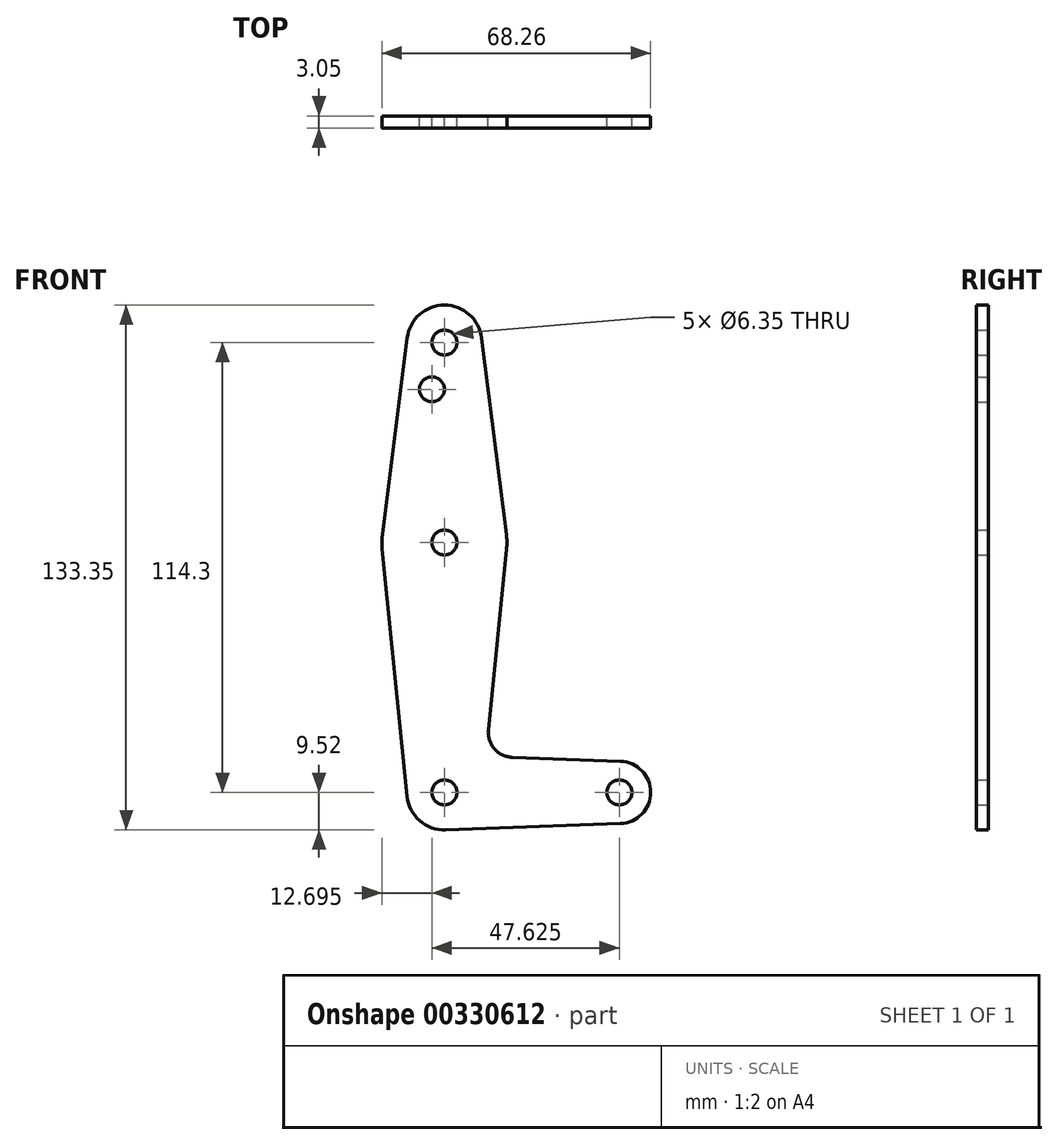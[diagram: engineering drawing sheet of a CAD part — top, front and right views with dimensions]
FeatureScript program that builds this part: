
annotation { "Feature Type Name" : "Feature", "Feature Type Description" : "" }
export const myFeature = defineFeature(function(context is Context, id is Id, definition is map)
    precondition{}
    {
        {
            var Q0;
            Q0=qCreatedBy(makeId("Front.planeOp"),FACE);
            var sketch = newSketch(context, id + "F0", { "sketchPlane" : qUnion([Q0])});
            skLineSegment(sketch, "E0", {"start": v(0, 114.3) * mm, "end": v(0, 0) * mm, "construction": true});
            skLineSegment(sketch, "E1", {"start": v(0, 0) * mm, "end": v(44.45, 0) * mm, "construction": true});
            skCircle(sketch, "E2", {"center": v(0, 114.3) * mm, "radius": 9.53 * mm});
            skCircle(sketch, "E3", {"center": v(0, 63.5) * mm, "radius": 15.88 * mm});
            skCircle(sketch, "E4", {"center": v(0, 0) * mm, "radius": 9.53 * mm});
            skCircle(sketch, "E5", {"center": v(44.45, 0) * mm, "radius": 7.94 * mm});
            skLineSegment(sketch, "E6", {"start": v(-9.45, 115.5) * mm, "end": v(-15.75, 65.48) * mm});
            skLineSegment(sketch, "E7", {"start": v(9.45, 115.5) * mm, "end": v(15.75, 65.48) * mm});
            skLineSegment(sketch, "E8", {"start": v(15.8, 61.91) * mm, "end": v(11.17, 15.9) * mm});
            skLineSegment(sketch, "E9", {"start": v(-15.8, 61.91) * mm, "end": v(-9.48, -0.95) * mm});
            skLineSegment(sketch, "E10", {"start": v(17.26, 8.91) * mm, "end": v(44.73, 7.93) * mm});
            skLineSegment(sketch, "E11", {"start": v(0.34, -9.52) * mm, "end": v(44.73, -7.93) * mm});
            skCircle(sketch, "E12", {"center": v(0, 114.3) * mm, "radius": 3.18 * mm});
            skCircle(sketch, "E13", {"center": v(0, 63.5) * mm, "radius": 3.18 * mm});
            skCircle(sketch, "E14", {"center": v(0, 0) * mm, "radius": 3.18 * mm});
            skCircle(sketch, "E15", {"center": v(44.45, 0) * mm, "radius": 3.18 * mm});
            skCircle(sketch, "E16", {"center": v(-3.18, 102.43) * mm, "radius": 3.18 * mm});
            skPoint(sketch, "E17.newPointB", {"position": v(0.34, 9.52) * mm});
            skArc(sketch, "E17.filletArc", {"start": v(11.17, 15.9) * mm, "mid": v(12.7, 11.09) * mm, "end": v(17.26, 8.91) * mm});
            skSolve(sketch);
        }
        {
            var Q0;
            Q0 = qSketchRegion(id + "F0", true);
            extrude(context, id + "F1", {"entities" : qUnion([Q0]), "depth" : 3.05 * mm});
        }
    });
